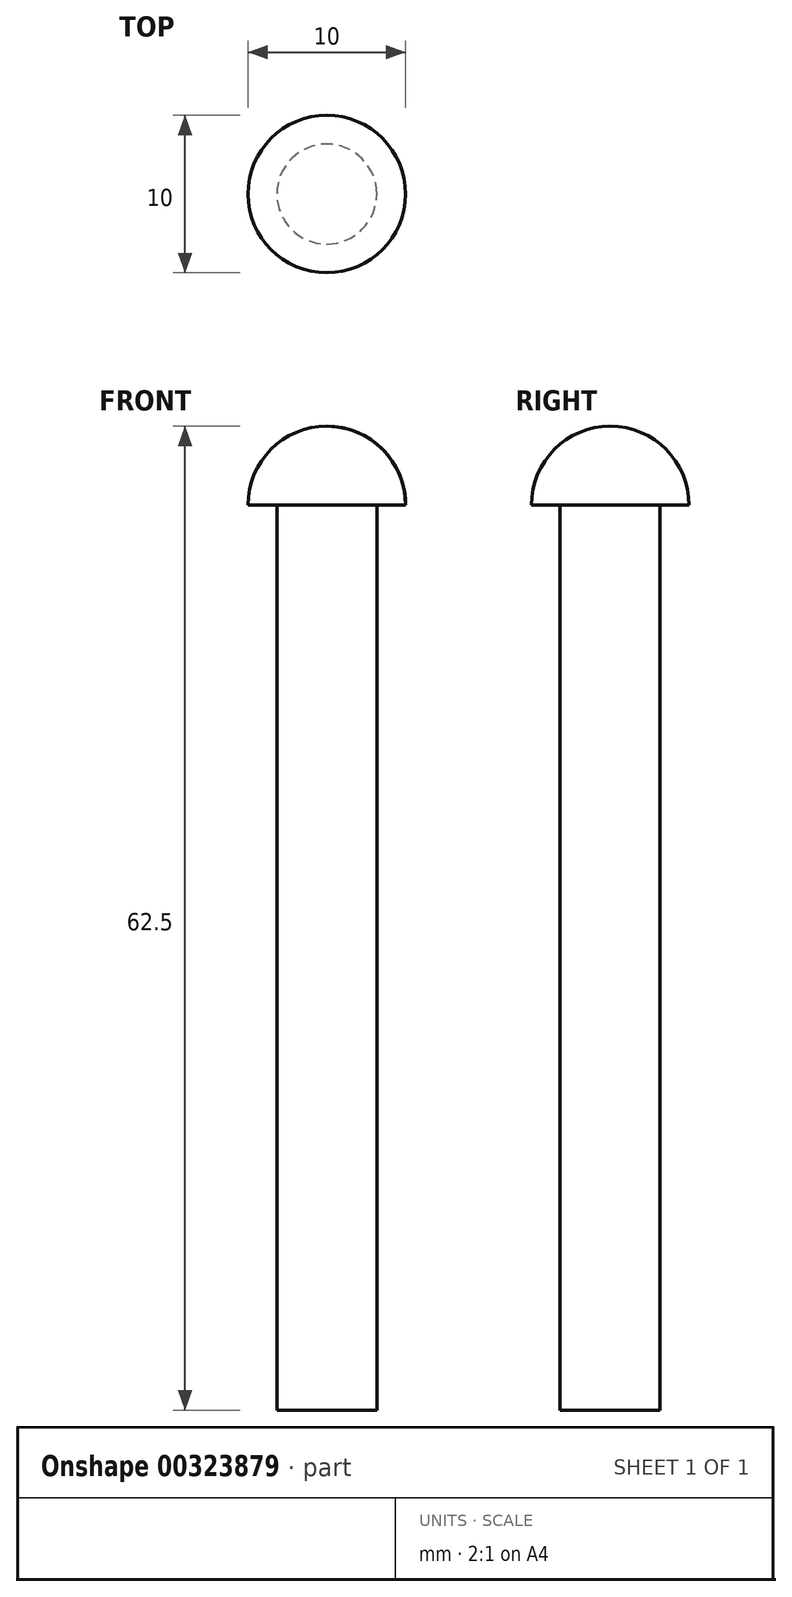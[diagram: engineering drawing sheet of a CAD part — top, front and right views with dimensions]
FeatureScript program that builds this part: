
annotation { "Feature Type Name" : "Feature", "Feature Type Description" : "" }
export const myFeature = defineFeature(function(context is Context, id is Id, definition is map)
    precondition{}
    {
        {
            var Q0;
            Q0=qCreatedBy(makeId("Top.planeOp"),FACE);
            var sketch = newSketch(context, id + "F0", { "sketchPlane" : qUnion([Q0])});
            skCircle(sketch, "E0", {"center": v(0, 0) * mm, "radius": 3.18 * mm});
            skSolve(sketch);
        }
        {
            var Q0;
            Q0=makeQuery(id+"F0.imprint","IMPRINT",FACE,{"disambiguationData":[TD([[makeQuery(id+"F0.imprint","IMPRINT",EDGE,{"derivedFrom":sQuery(id+"F0.wireOp",EDGE,"E0")}),1.0]])]});
            extrude(context, id + "F1", {"entities" : qUnion([Q0]), "depth" : 57.5 * mm});
        }
        {
            var Q0;
            Q0=makeQuery(id+"F1.opExtrude","CAP_FACE",FACE,{"disambiguationData":[OSD([sQuery(id+"F0.wireOp",EDGE,"E0")])],"isStart":false});
            var sketch = newSketch(context, id + "F2", { "sketchPlane" : qUnion([Q0])});
            skCircle(sketch, "E1", {"center": v(0, 0) * mm, "radius": 5 * mm});
            skSolve(sketch);
        }
        {
            var Q0;
            Q0=makeQuery(id+"F2.imprint","IMPRINT",FACE,{"disambiguationData":[TD([[makeQuery(id+"F2.imprint","IMPRINT",EDGE,{"derivedFrom":makeQuery(id+"F1.opExtrude","CAP_EDGE",EDGE,{"disambiguationData":[OSD([sQuery(id+"F0.wireOp",EDGE,"E0")])],"isStart":false})}),1.0]])]});
            var Q1;
            Q1=makeQuery(id+"F2.imprint","IMPRINT",FACE,{"disambiguationData":[TD([[makeQuery(id+"F2.imprint","IMPRINT",EDGE,{"derivedFrom":sQuery(id+"F2.wireOp",EDGE,"E1")}),1.0]])]});
            extrude(context, id + "F3", {"entities" : qUnion([Q0, Q1]), "operationType" : NewBodyOperationType.ADD, "depth" : 5 * mm});
        }
        {
            var Q0;
            Q0=makeQuery(id+"F3.opExtrude","CAP_EDGE",EDGE,{"disambiguationData":[OSD([sQuery(id+"F2.wireOp",EDGE,"E1")])],"isStart":false});
            fillet(context, id + "F4", {"entities" : qUnion([Q0]), "radius" : 5 * mm, "tangentPropagation" : true, "allowEdgeOverflow" : false});
        }
    });
